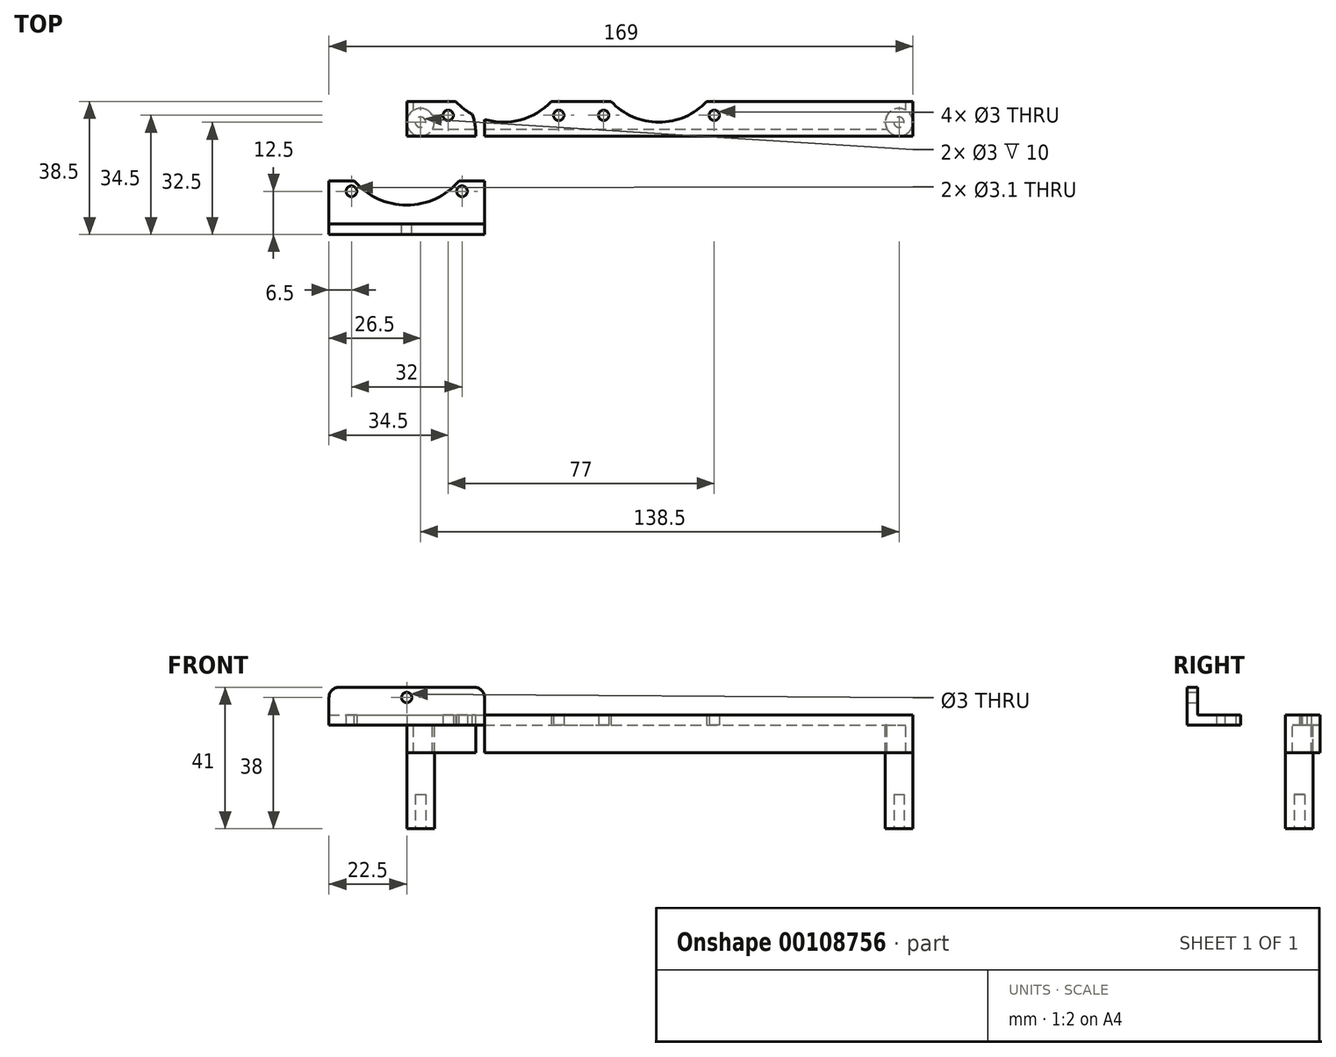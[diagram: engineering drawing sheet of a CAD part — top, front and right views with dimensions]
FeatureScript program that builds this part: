
annotation { "Feature Type Name" : "Feature", "Feature Type Description" : "" }
export const myFeature = defineFeature(function(context is Context, id is Id, definition is map)
    precondition{}
    {
        {
            var Q0;
            Q0=qCreatedBy(makeId("Top.planeOp"),FACE);
            var sketch = newSketch(context, id + "F0", { "sketchPlane" : qUnion([Q0])});
            skLineSegment(sketch, "E0.bottom", {"start": v(0, 0) * mm, "end": v(146.5, 0) * mm});
            skLineSegment(sketch, "E0.top", {"start": v(0, 10) * mm, "end": v(14.14, 10) * mm});
            skLineSegment(sketch, "E0.left", {"start": v(0, 0) * mm, "end": v(0, 10) * mm});
            skLineSegment(sketch, "E0.right", {"start": v(146.5, 0) * mm, "end": v(146.5, 10) * mm});
            skCircle(sketch, "E1", {"center": v(12, 6) * mm, "radius": 1.5 * mm});
            skCircle(sketch, "E2", {"center": v(44, 6) * mm, "radius": 1.5 * mm});
            skLineSegment(sketch, "E3", {"start": v(12, 6) * mm, "end": v(44, 6) * mm, "construction": true});
            skLineSegment(sketch, "E4", {"start": v(28, 6) * mm, "end": v(28, 23) * mm, "construction": true});
            skLineSegment(sketch, "E5", {"start": v(40.22, 10) * mm, "end": v(40.22, 10) * mm});
            skArc(sketch, "E6", {"start": v(14.14, 10) * mm, "mid": v(28, 4) * mm, "end": v(41.86, 10) * mm});
            skLineSegment(sketch, "E7.trimOffspring", {"start": v(41.86, 10) * mm, "end": v(59.14, 10) * mm});
            skLineSegment(sketch, "E8.bottom", {"start": v(8, 3) * mm, "end": v(48, 3) * mm, "construction": true});
            skLineSegment(sketch, "E8.top", {"start": v(8, 43) * mm, "end": v(48, 43) * mm, "construction": true});
            skLineSegment(sketch, "E8.left", {"start": v(8, 3) * mm, "end": v(8, 43) * mm, "construction": true});
            skLineSegment(sketch, "E8.right", {"start": v(48, 3) * mm, "end": v(48, 43) * mm, "construction": true});
            skLineSegment(sketch, "E9", {"start": v(8, 23) * mm, "end": v(28, 23) * mm, "construction": true});
            skLineSegment(sketch, "E10", {"start": v(28, 23) * mm, "end": v(28, 3) * mm, "construction": true});
            skCircle(sketch, "E11.1.0.0", {"center": v(89, 6) * mm, "radius": 1.5 * mm});
            skCircle(sketch, "E11.1.0.1", {"center": v(57, 6) * mm, "radius": 1.5 * mm});
            skArc(sketch, "E11.1.0.2", {"start": v(59.14, 10) * mm, "mid": v(73, 4) * mm, "end": v(86.86, 10) * mm});
            skLineSegment(sketch, "E11.1.0.3", {"start": v(57, 6) * mm, "end": v(89, 6) * mm, "construction": true});
            skLineSegment(sketch, "E11.direction1", {"start": v(12, 6) * mm, "end": v(57, 6) * mm, "construction": true});
            skLineSegment(sketch, "E12.trimOffspring", {"start": v(86.86, 10) * mm, "end": v(146.5, 10) * mm});
            skSolve(sketch);
        }
        {
            var Q0;
            Q0=makeQuery(id+"F0.imprint","IMPRINT",FACE,{"disambiguationData":[TD([[makeQuery(id+"F0.imprint","IMPRINT",EDGE,{"derivedFrom":sQuery(id+"F0.wireOp",EDGE,"E0.bottom")}),1.0]])]});
            extrude(context, id + "F1", {"entities" : qUnion([Q0]), "depth" : 3 * mm});
        }
        {
            var Q0;
            Q0=makeQuery(id+"F1.opExtrude","CAP_FACE",FACE,{"disambiguationData":[OSD([sQuery(id+"F0.wireOp",EDGE,"E0.bottom"),sQuery(id+"F0.wireOp",EDGE,"E0.top"),sQuery(id+"F0.wireOp",EDGE,"E0.left"),sQuery(id+"F0.wireOp",EDGE,"E0.right"),sQuery(id+"F0.wireOp",EDGE,"E1"),sQuery(id+"F0.wireOp",EDGE,"E2"),sQuery(id+"F0.wireOp",EDGE,"E6"),sQuery(id+"F0.wireOp",EDGE,"E7.trimOffspring"),sQuery(id+"F0.wireOp",EDGE,"E11.1.0.0"),sQuery(id+"F0.wireOp",EDGE,"E11.1.0.1"),sQuery(id+"F0.wireOp",EDGE,"E11.1.0.2"),sQuery(id+"F0.wireOp",EDGE,"E12.trimOffspring")])],"isStart":true});
            var sketch = newSketch(context, id + "F2", { "sketchPlane" : qUnion([Q0])});
            skLineSegment(sketch, "E13.0", {"start": v(0, 0) * mm, "end": v(146.5, 0) * mm});
            skLineSegment(sketch, "E13.1", {"start": v(0, 0) * mm, "end": v(0, -10) * mm});
            skLineSegment(sketch, "E13.2", {"start": v(146.5, 0) * mm, "end": v(146.5, -10) * mm});
            skLineSegment(sketch, "E14.0", {"start": v(144.5, -2) * mm, "end": v(144.5, -10) * mm});
            skLineSegment(sketch, "E14.1", {"start": v(2, -2) * mm, "end": v(144.5, -2) * mm});
            skLineSegment(sketch, "E14.2", {"start": v(2, -2) * mm, "end": v(2, -10) * mm});
            skLineSegment(sketch, "E15", {"start": v(2, -10) * mm, "end": v(0, -10) * mm});
            skLineSegment(sketch, "E16", {"start": v(146.5, -10) * mm, "end": v(144.5, -10) * mm});
            skSolve(sketch);
        }
        {
            var Q0;
            Q0=makeQuery(id+"F2.imprint","IMPRINT",FACE,{"disambiguationData":[TD([[makeQuery(id+"F2.imprint","IMPRINT",EDGE,{"derivedFrom":sQuery(id+"F2.wireOp",EDGE,"E13.0")}),-1.0]])]});
            extrude(context, id + "F3", {"entities" : qUnion([Q0]), "operationType" : NewBodyOperationType.ADD, "depth" : 8 * mm});
        }
        {
            var Q0;
            Q0=makeQuery(id+"F1.opExtrude","CAP_FACE",FACE,{"disambiguationData":[OSD([sQuery(id+"F0.wireOp",EDGE,"E0.bottom"),sQuery(id+"F0.wireOp",EDGE,"E0.top"),sQuery(id+"F0.wireOp",EDGE,"E0.left"),sQuery(id+"F0.wireOp",EDGE,"E0.right"),sQuery(id+"F0.wireOp",EDGE,"E1"),sQuery(id+"F0.wireOp",EDGE,"E2"),sQuery(id+"F0.wireOp",EDGE,"E6"),sQuery(id+"F0.wireOp",EDGE,"E7.trimOffspring"),sQuery(id+"F0.wireOp",EDGE,"E11.1.0.0"),sQuery(id+"F0.wireOp",EDGE,"E11.1.0.1"),sQuery(id+"F0.wireOp",EDGE,"E11.1.0.2"),sQuery(id+"F0.wireOp",EDGE,"E12.trimOffspring")])],"isStart":true});
            var sketch = newSketch(context, id + "F4", { "sketchPlane" : qUnion([Q0])});
            skCircle(sketch, "E17", {"center": v(142.5, -4) * mm, "radius": 4 * mm});
            skCircle(sketch, "E18", {"center": v(4, -4) * mm, "radius": 4 * mm});
            skSolve(sketch);
        }
        {
            var Q0;
            {var subQ0=sQuery(id+"F4.wireOp",EDGE,"E18");var subQ1=makeQuery(id+"F3.opExtrude","CAP_EDGE",EDGE,{"disambiguationData":[OSD([sQuery(id+"F2.wireOp",EDGE,"E14.1")])],"isStart":true});var subQ2=makeQuery(id+"F4.imprint","INTERSECT",VERTEX,{"derivedFrom":[subQ1,subQ0]});Q0=makeQuery(id+"F4.imprint","IMPRINT",FACE,{"disambiguationData":[TD([[makeQuery(id+"F4.imprint","IMPRINT",EDGE,{"disambiguationData":[TD([[subQ2,1.0]])],"derivedFrom":subQ0}),1.0]])]});}
            var Q1;
            {var subQ0=sQuery(id+"F4.wireOp",EDGE,"E17");var subQ1=makeQuery(id+"F3.opExtrude","CAP_EDGE",EDGE,{"disambiguationData":[OSD([sQuery(id+"F2.wireOp",EDGE,"E14.0")])],"isStart":true});var subQ2=makeQuery(id+"F4.imprint","INTERSECT",VERTEX,{"derivedFrom":[subQ1,subQ0]});Q1=makeQuery(id+"F4.imprint","IMPRINT",FACE,{"disambiguationData":[TD([[makeQuery(id+"F4.imprint","IMPRINT",EDGE,{"disambiguationData":[TD([[subQ2,1.0]])],"derivedFrom":subQ0}),1.0]])]});}
            var Q2;
            {var subQ0=sQuery(id+"F4.wireOp",EDGE,"E18");var subQ1=makeQuery(id+"F3.opExtrude","CAP_EDGE",EDGE,{"disambiguationData":[OSD([sQuery(id+"F2.wireOp",EDGE,"E14.1")])],"isStart":true});var subQ2=makeQuery(id+"F4.imprint","INTERSECT",VERTEX,{"derivedFrom":[subQ1,subQ0]});Q2=makeQuery(id+"F4.imprint","IMPRINT",FACE,{"disambiguationData":[TD([[makeQuery(id+"F4.imprint","IMPRINT",EDGE,{"disambiguationData":[TD([[subQ2,-1.0]])],"derivedFrom":subQ0}),1.0]])]});}
            var Q3;
            {var subQ0=sQuery(id+"F4.wireOp",EDGE,"E17");var subQ1=makeQuery(id+"F3.opExtrude","CAP_EDGE",EDGE,{"disambiguationData":[OSD([sQuery(id+"F2.wireOp",EDGE,"E14.0")])],"isStart":true});var subQ2=makeQuery(id+"F4.imprint","INTERSECT",VERTEX,{"derivedFrom":[subQ1,subQ0]});Q3=makeQuery(id+"F4.imprint","IMPRINT",FACE,{"disambiguationData":[TD([[makeQuery(id+"F4.imprint","IMPRINT",EDGE,{"disambiguationData":[TD([[subQ2,-1.0]])],"derivedFrom":subQ0}),1.0]])]});}
            extrude(context, id + "F5", {"entities" : qUnion([Q0, Q1, Q2, Q3]), "operationType" : NewBodyOperationType.ADD, "depth" : 30 * mm});
        }
        {
            var Q0;
            Q0=makeQuery(id+"F5.opExtrude","CAP_FACE",FACE,{"disambiguationData":[OSD([sQuery(id+"F4.wireOp",EDGE,"E18")])],"isStart":false});
            var sketch = newSketch(context, id + "F6", { "sketchPlane" : qUnion([Q0])});
            skCircle(sketch, "E19", {"center": v(4, -4) * mm, "radius": 1.5 * mm});
            skCircle(sketch, "E20", {"center": v(142.5, -4) * mm, "radius": 1.5 * mm});
            skSolve(sketch);
        }
        {
            var Q0;
            Q0=makeQuery(id+"F6.imprint","IMPRINT",FACE,{"disambiguationData":[TD([[makeQuery(id+"F6.imprint","IMPRINT",EDGE,{"derivedFrom":sQuery(id+"F6.wireOp",EDGE,"E20")}),1.0]])]});
            var Q1;
            Q1=makeQuery(id+"F6.imprint","IMPRINT",FACE,{"disambiguationData":[TD([[makeQuery(id+"F6.imprint","IMPRINT",EDGE,{"derivedFrom":sQuery(id+"F6.wireOp",EDGE,"E19")}),1.0]])]});
            extrude(context, id + "F7", {"entities" : qUnion([Q0, Q1]), "operationType" : NewBodyOperationType.REMOVE, "oppositeDirection" : true, "depth" : 10 * mm});
        }
        {
            var Q0;
            Q0=qCreatedBy(makeId("Top.planeOp"),FACE);
            var sketch = newSketch(context, id + "F8", { "sketchPlane" : qUnion([Q0])});
            skCircle(sketch, "E21", {"center": v(0, 0) * mm, "radius": 20 * mm});
            skLineSegment(sketch, "E22.bottom", {"start": v(22.5, 22.5) * mm, "end": v(-22.5, 22.5) * mm});
            skLineSegment(sketch, "E22.top", {"start": v(22.5, -22.5) * mm, "end": v(-22.5, -22.5) * mm});
            skLineSegment(sketch, "E22.left", {"start": v(22.5, 22.5) * mm, "end": v(22.5, -22.5) * mm});
            skLineSegment(sketch, "E22.right", {"start": v(-22.5, 22.5) * mm, "end": v(-22.5, -22.5) * mm});
            skCircle(sketch, "E23", {"center": v(16, 16) * mm, "radius": 1.55 * mm});
            skCircle(sketch, "E24.MirrorC", {"center": v(-16, 16) * mm, "radius": 1.55 * mm});
            skCircle(sketch, "E25.MirrorC", {"center": v(-16, -16) * mm, "radius": 1.55 * mm});
            skCircle(sketch, "E26.MirrorC", {"center": v(16, -16) * mm, "radius": 1.55 * mm});
            skSolve(sketch);
        }
        {
            var Q0;
            Q0=makeQuery(id+"F8.imprint","IMPRINT",FACE,{"disambiguationData":[TD([[makeQuery(id+"F8.imprint","IMPRINT",EDGE,{"derivedFrom":sQuery(id+"F8.wireOp",EDGE,"E21")}),-1.0]])]});
            extrude(context, id + "F9", {"entities" : qUnion([Q0]), "depth" : 3 * mm});
        }
        {
            var Q0;
            Q0=qCreatedBy(makeId("Top.planeOp"),FACE);
            var sketch = newSketch(context, id + "F10", { "sketchPlane" : qUnion([Q0])});
            skLineSegment(sketch, "E27.0", {"start": v(22.5, -22.5) * mm, "end": v(-22.5, -22.5) * mm});
            skLineSegment(sketch, "E28", {"start": v(-22.5, -22.5) * mm, "end": v(-22.5, -28.5) * mm});
            skLineSegment(sketch, "E29", {"start": v(-22.5, -28.5) * mm, "end": v(22.5, -28.5) * mm});
            skLineSegment(sketch, "E30", {"start": v(22.5, -28.5) * mm, "end": v(22.5, -22.5) * mm});
            skSolve(sketch);
        }
        {
            var Q0;
            Q0=makeQuery(id+"F10.imprint","IMPRINT",FACE,{"disambiguationData":[TD([[makeQuery(id+"F10.imprint","IMPRINT",EDGE,{"derivedFrom":sQuery(id+"F10.wireOp",EDGE,"E27.0")}),1.0]])]});
            var Q1;
            Q1=makeQuery(id+"F9.opExtrude","CAP_FACE",FACE,{"disambiguationData":[OSD([sQuery(id+"F8.wireOp",EDGE,"E21"),sQuery(id+"F8.wireOp",EDGE,"E22.bottom"),sQuery(id+"F8.wireOp",EDGE,"E22.top"),sQuery(id+"F8.wireOp",EDGE,"E22.left"),sQuery(id+"F8.wireOp",EDGE,"E22.right"),sQuery(id+"F8.wireOp",EDGE,"E24.MirrorC"),sQuery(id+"F8.wireOp",EDGE,"E23"),sQuery(id+"F8.wireOp",EDGE,"E25.MirrorC"),sQuery(id+"F8.wireOp",EDGE,"E26.MirrorC")])],"isStart":false});
            extrude(context, id + "F11", {"entities" : qUnion([Q0]), "operationType" : NewBodyOperationType.ADD, "endBound" : BoundingType.UP_TO_SURFACE, "endBoundEntityFace" : qUnion([Q1]), "depth" : 25 * mm});
        }
        {
            var Q0;
            {var subQ0=sQuery(id+"F8.wireOp",EDGE,"E26.MirrorC");var subQ1=sQuery(id+"F8.wireOp",EDGE,"E25.MirrorC");var subQ2=sQuery(id+"F8.wireOp",EDGE,"E23");var subQ3=sQuery(id+"F8.wireOp",EDGE,"E24.MirrorC");var subQ4=sQuery(id+"F8.wireOp",EDGE,"E22.right");var subQ5=sQuery(id+"F8.wireOp",EDGE,"E22.left");var subQ6=sQuery(id+"F8.wireOp",EDGE,"E22.top");var subQ7=sQuery(id+"F8.wireOp",EDGE,"E22.bottom");var subQ8=sQuery(id+"F8.wireOp",EDGE,"E21");Q0=makeQuery(id+"F11.boolean.opBoolean","MERGE",FACE,{"derivedFrom":[makeQuery(id+"F9.opExtrude","CAP_FACE",FACE,{"disambiguationData":[OSD([subQ8,subQ7,subQ6,subQ5,subQ4,subQ3,subQ2,subQ1,subQ0])],"isStart":false}),makeQuery(id+"F11.opExtrude","CAP_FACE",FACE,{"disambiguationData":[OSD([subQ8,subQ7,subQ6,subQ5,subQ4,subQ3,subQ2,subQ1,subQ0])],"isStart":false})]});}
            var sketch = newSketch(context, id + "F12", { "sketchPlane" : qUnion([Q0])});
            skLineSegment(sketch, "E31.bottom", {"start": v(-22.5, -28.5) * mm, "end": v(22.5, -28.5) * mm});
            skLineSegment(sketch, "E31.top", {"start": v(-22.5, -25.5) * mm, "end": v(22.5, -25.5) * mm});
            skLineSegment(sketch, "E31.left", {"start": v(-22.5, -28.5) * mm, "end": v(-22.5, -25.5) * mm});
            skLineSegment(sketch, "E31.right", {"start": v(22.5, -28.5) * mm, "end": v(22.5, -25.5) * mm});
            skSolve(sketch);
        }
        {
            var Q0;
            Q0=makeQuery(id+"F12.imprint","IMPRINT",FACE,{"disambiguationData":[TD([[makeQuery(id+"F12.imprint","IMPRINT",EDGE,{"derivedFrom":sQuery(id+"F12.wireOp",EDGE,"E31.bottom")}),1.0]])]});
            extrude(context, id + "F13", {"entities" : qUnion([Q0]), "operationType" : NewBodyOperationType.ADD, "depth" : 8 * mm});
        }
        {
            var Q0;
            Q0=makeQuery(id+"F13.opExtrude","SWEPT_FACE",FACE,{"disambiguationData":[OSD([sQuery(id+"F12.wireOp",EDGE,"E31.top")])]});
            var sketch = newSketch(context, id + "F14", { "sketchPlane" : qUnion([Q0])});
            skCircle(sketch, "E32", {"center": v(0, 8) * mm, "radius": 1.5 * mm});
            skCircle(sketch, "E33", {"center": v(0, 8) * mm, "radius": 3 * mm});
            skSolve(sketch);
        }
        {
            var Q0;
            Q0=makeQuery(id+"F14.imprint","IMPRINT",FACE,{"disambiguationData":[TD([[makeQuery(id+"F14.imprint","IMPRINT",EDGE,{"derivedFrom":sQuery(id+"F14.wireOp",EDGE,"E32")}),1.0]])]});
            extrude(context, id + "F15", {"entities" : qUnion([Q0]), "operationType" : NewBodyOperationType.REMOVE, "endBound" : BoundingType.THROUGH_ALL, "oppositeDirection" : true, "depth" : 25 * mm});
        }
        {
            var Q0;
            {var subQ0=sQuery(id+"F8.wireOp",EDGE,"E26.MirrorC");var subQ1=sQuery(id+"F8.wireOp",EDGE,"E25.MirrorC");var subQ2=sQuery(id+"F8.wireOp",EDGE,"E23");var subQ3=sQuery(id+"F8.wireOp",EDGE,"E24.MirrorC");var subQ4=sQuery(id+"F8.wireOp",EDGE,"E22.right");var subQ5=sQuery(id+"F8.wireOp",EDGE,"E22.left");var subQ6=sQuery(id+"F8.wireOp",EDGE,"E22.top");var subQ7=sQuery(id+"F8.wireOp",EDGE,"E22.bottom");var subQ8=sQuery(id+"F8.wireOp",EDGE,"E21");Q0=makeQuery(id+"F11.boolean.opBoolean","MERGE",FACE,{"derivedFrom":[makeQuery(id+"F9.opExtrude","CAP_FACE",FACE,{"disambiguationData":[OSD([subQ8,subQ7,subQ6,subQ5,subQ4,subQ3,subQ2,subQ1,subQ0])],"isStart":false}),makeQuery(id+"F11.opExtrude","CAP_FACE",FACE,{"disambiguationData":[OSD([subQ8,subQ7,subQ6,subQ5,subQ4,subQ3,subQ2,subQ1,subQ0])],"isStart":false})]});}
            var sketch = newSketch(context, id + "F16", { "sketchPlane" : qUnion([Q0])});
            skLineSegment(sketch, "E34.bottom", {"start": v(-22.5, -13) * mm, "end": v(22.5, -13) * mm});
            skLineSegment(sketch, "E34.top", {"start": v(-22.5, 22.5) * mm, "end": v(22.5, 22.5) * mm});
            skLineSegment(sketch, "E34.left", {"start": v(-22.5, -13) * mm, "end": v(-22.5, 22.5) * mm});
            skLineSegment(sketch, "E34.right", {"start": v(22.5, -13) * mm, "end": v(22.5, 22.5) * mm});
            skSolve(sketch);
        }
        {
            var Q0;
            Q0=makeQuery(id+"F16.imprint","IMPRINT",FACE,{"disambiguationData":[TD([[makeQuery(id+"F16.imprint","IMPRINT",EDGE,{"derivedFrom":sQuery(id+"F16.wireOp",EDGE,"E34.top")}),1.0]])]});
            extrude(context, id + "F17", {"entities" : qUnion([Q0]), "operationType" : NewBodyOperationType.REMOVE, "endBound" : BoundingType.THROUGH_ALL, "oppositeDirection" : true, "depth" : 25 * mm});
        }
        {
            var Q0;
            Q0=makeQuery(id+"F17.boolean.opBoolean","COPY",EDGE,{"derivedFrom":makeQuery(id+"F17.opExtrude","SWEPT_EDGE",EDGE,{"disambiguationData":[OSD([sQuery(id+"F8.wireOp",EDGE,"E21"),sQuery(id+"F8.wireOp",EDGE,"E22.bottom"),sQuery(id+"F8.wireOp",EDGE,"E22.top"),sQuery(id+"F8.wireOp",EDGE,"E22.left"),sQuery(id+"F8.wireOp",EDGE,"E22.right"),sQuery(id+"F8.wireOp",EDGE,"E24.MirrorC"),sQuery(id+"F8.wireOp",EDGE,"E23"),sQuery(id+"F8.wireOp",EDGE,"E25.MirrorC"),sQuery(id+"F8.wireOp",EDGE,"E26.MirrorC"),sQuery(id+"F10.wireOp",EDGE,"E30"),sQuery(id+"F16.wireOp",EDGE,"E34.bottom"),sQuery(id+"F16.wireOp",EDGE,"E34.right")])]})});
            var Q1;
            Q1=makeQuery(id+"F17.boolean.opBoolean","COPY",EDGE,{"derivedFrom":makeQuery(id+"F17.opExtrude","SWEPT_EDGE",EDGE,{"disambiguationData":[OSD([sQuery(id+"F8.wireOp",EDGE,"E21"),sQuery(id+"F8.wireOp",EDGE,"E22.bottom"),sQuery(id+"F8.wireOp",EDGE,"E22.top"),sQuery(id+"F8.wireOp",EDGE,"E22.left"),sQuery(id+"F8.wireOp",EDGE,"E22.right"),sQuery(id+"F8.wireOp",EDGE,"E24.MirrorC"),sQuery(id+"F8.wireOp",EDGE,"E23"),sQuery(id+"F8.wireOp",EDGE,"E25.MirrorC"),sQuery(id+"F8.wireOp",EDGE,"E26.MirrorC"),sQuery(id+"F10.wireOp",EDGE,"E28"),sQuery(id+"F16.wireOp",EDGE,"E34.bottom"),sQuery(id+"F16.wireOp",EDGE,"E34.left")])]})});
            var Q2;
            Q2=makeQuery(id+"F13.opExtrude","CAP_EDGE",EDGE,{"disambiguationData":[OSD([sQuery(id+"F12.wireOp",EDGE,"E31.right")])],"isStart":false});
            var Q3;
            Q3=makeQuery(id+"F13.opExtrude","CAP_EDGE",EDGE,{"disambiguationData":[OSD([sQuery(id+"F12.wireOp",EDGE,"E31.left")])],"isStart":false});
            fillet(context, id + "F18", {"entities" : qUnion([Q0, Q1, Q2, Q3]), "radius" : 3 * mm, "tangentPropagation" : true, "allowEdgeOverflow" : false});
        }
    });
